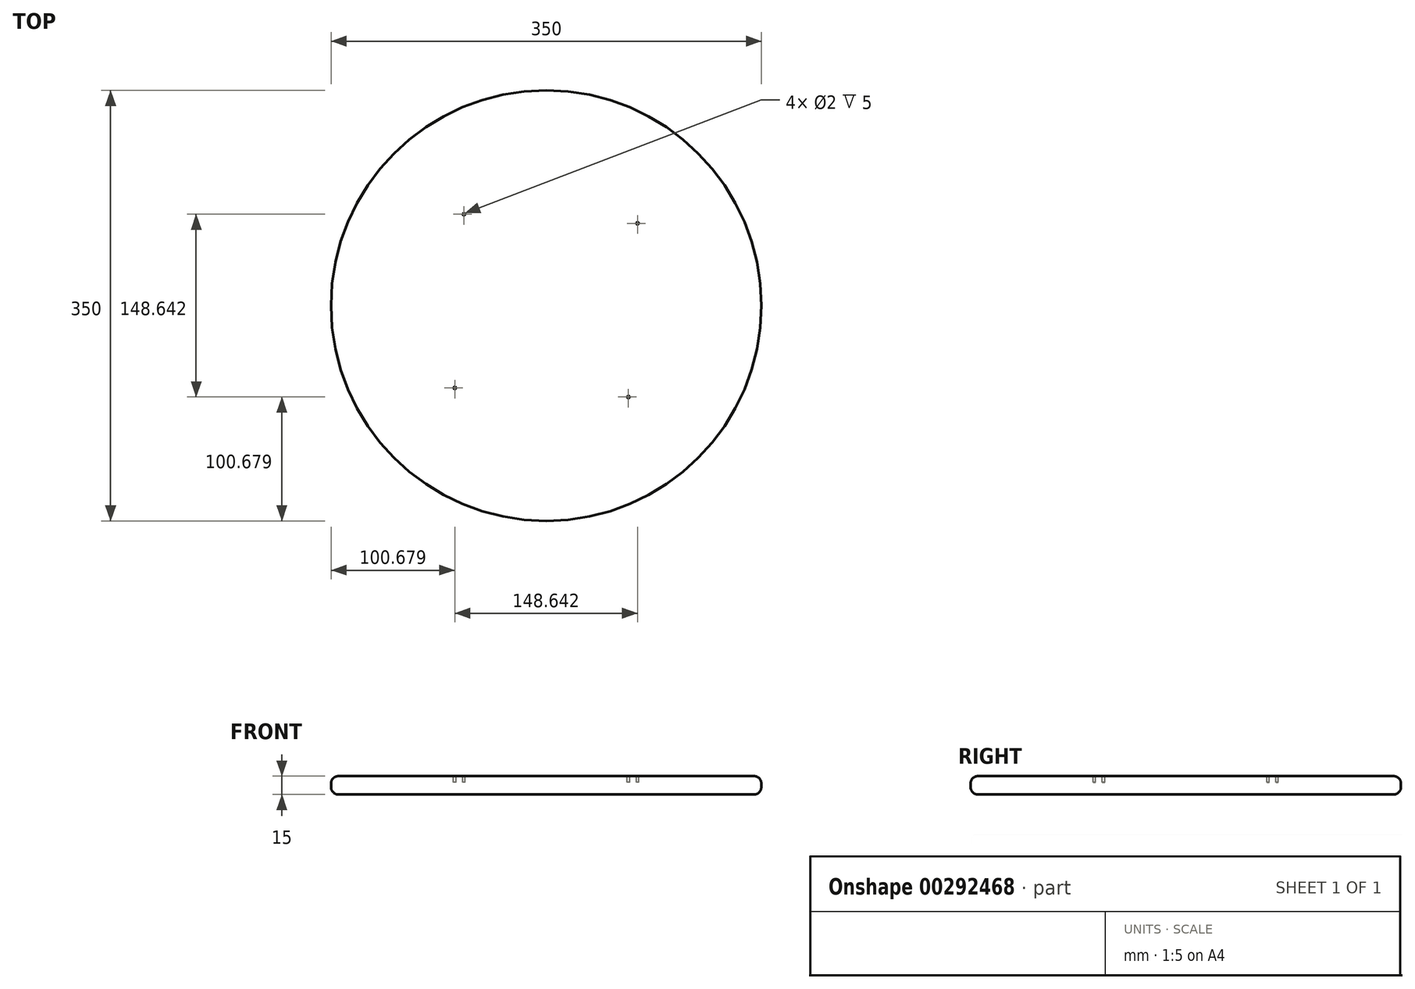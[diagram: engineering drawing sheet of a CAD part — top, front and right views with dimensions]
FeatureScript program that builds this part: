
annotation { "Feature Type Name" : "Feature", "Feature Type Description" : "" }
export const myFeature = defineFeature(function(context is Context, id is Id, definition is map)
    precondition{}
    {
        {
            var Q0;
            Q0=qCreatedBy(makeId("Top.planeOp"),FACE);
            var sketch = newSketch(context, id + "F0", { "sketchPlane" : qUnion([Q0])});
            skCircle(sketch, "E0", {"center": v(0, 0) * mm, "radius": 175 * mm});
            skSolve(sketch);
        }
        {
            var Q0;
            Q0 = qSketchRegion(id + "F0", true);
            extrude(context, id + "F1", {"entities" : qUnion([Q0]), "depth" : 15 * mm});
        }
        {
            var Q0;
            Q0=makeQuery(id+"F1.opExtrude","CAP_EDGE",EDGE,{"disambiguationData":[OSD([sQuery(id+"F0.wireOp",EDGE,"E0")])],"isStart":false});
            var Q1;
            Q1=makeQuery(id+"F1.opExtrude","CAP_EDGE",EDGE,{"disambiguationData":[OSD([sQuery(id+"F0.wireOp",EDGE,"E0")])],"isStart":true});
            fillet(context, id + "F2", {"entities" : qUnion([Q0, Q1]), "radius" : 6 * mm, "tangentPropagation" : true, "allowEdgeOverflow" : false});
        }
        {
            var Q0;
            Q0=makeQuery(id+"F1.opExtrude","CAP_FACE",FACE,{"disambiguationData":[OSD([sQuery(id+"F0.wireOp",EDGE,"E0")])],"isStart":false});
            var sketch = newSketch(context, id + "F3", { "sketchPlane" : qUnion([Q0])});
            skCircle(sketch, "E1", {"center": v(-66.9, 74.32) * mm, "radius": 1 * mm});
            skCircle(sketch, "E2.1.0", {"center": v(-74.32, -66.9) * mm, "radius": 1 * mm});
            skCircle(sketch, "E2.2.0", {"center": v(66.9, -74.32) * mm, "radius": 1 * mm});
            skCircle(sketch, "E2.3.0", {"center": v(74.32, 66.9) * mm, "radius": 1 * mm});
            skPoint(sketch, "E2.center", {"position": v(0, 0) * mm});
            skSolve(sketch);
        }
        {
            var Q0;
            Q0 = qSketchRegion(id + "F3", true);
            extrude(context, id + "F4", {"entities" : qUnion([Q0]), "operationType" : NewBodyOperationType.REMOVE, "oppositeDirection" : true, "depth" : 5 * mm});
        }
    });
